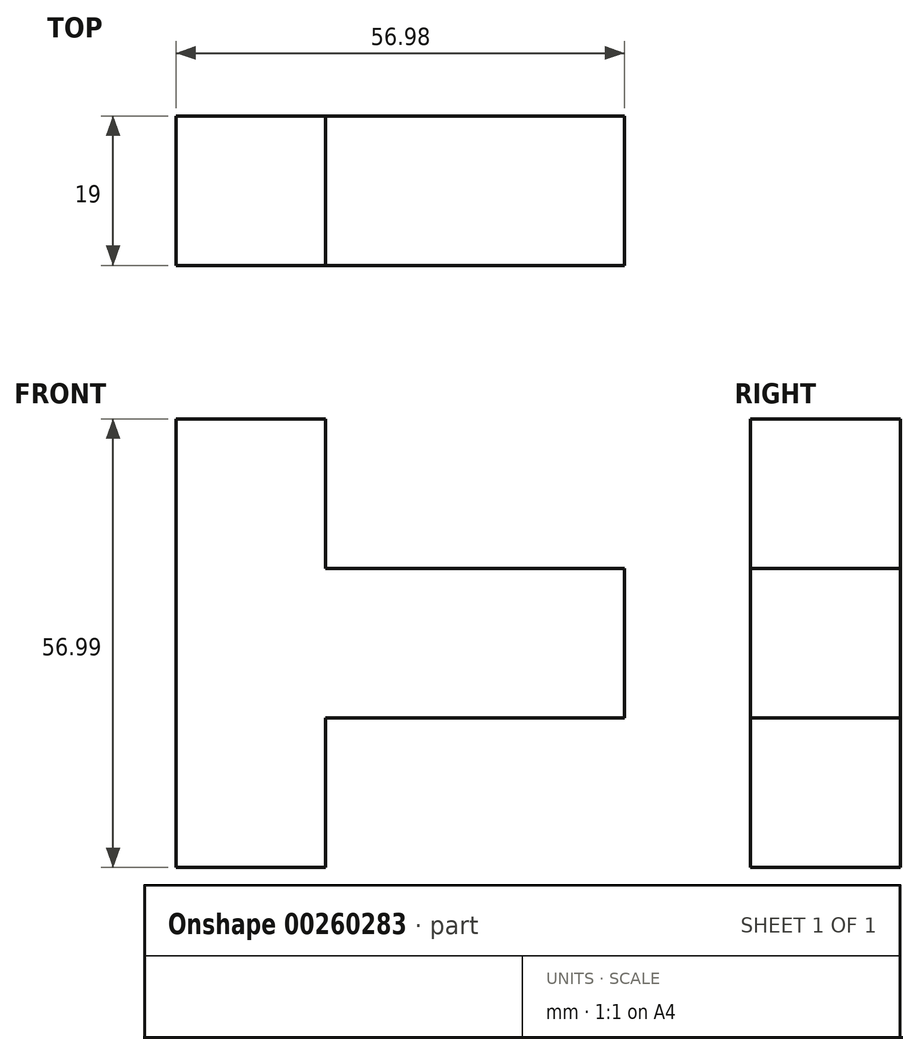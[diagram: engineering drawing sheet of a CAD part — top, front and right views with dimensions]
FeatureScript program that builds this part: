
annotation { "Feature Type Name" : "Feature", "Feature Type Description" : "" }
export const myFeature = defineFeature(function(context is Context, id is Id, definition is map)
    precondition{}
    {
        {
            var Q0;
            Q0=qCreatedBy(makeId("Front.planeOp"),FACE);
            var sketch = newSketch(context, id + "F0", { "sketchPlane" : qUnion([Q0])});
            skLineSegment(sketch, "E0.bottom", {"start": v(-67.92, 0) * mm, "end": v(-48.93, 0) * mm});
            skLineSegment(sketch, "E0.top", {"start": v(-67.92, -19) * mm, "end": v(-48.93, -19) * mm});
            skLineSegment(sketch, "E0.left", {"start": v(-67.92, 0) * mm, "end": v(-67.92, -19) * mm});
            skLineSegment(sketch, "E0.right", {"start": v(-48.93, 0) * mm, "end": v(-48.93, -19) * mm});
            skLineSegment(sketch, "E1.top", {"start": v(-67.92, -38) * mm, "end": v(-48.93, -38) * mm});
            skLineSegment(sketch, "E1.left", {"start": v(-67.92, -19) * mm, "end": v(-67.92, -38) * mm});
            skLineSegment(sketch, "E1.right", {"start": v(-48.93, -19) * mm, "end": v(-48.93, -38) * mm});
            skLineSegment(sketch, "E2.top", {"start": v(-67.92, 19) * mm, "end": v(-48.93, 19) * mm});
            skLineSegment(sketch, "E2.left", {"start": v(-67.92, 0) * mm, "end": v(-67.92, 19) * mm});
            skLineSegment(sketch, "E2.right", {"start": v(-48.93, 0) * mm, "end": v(-48.93, 19) * mm});
            skLineSegment(sketch, "E3.bottom", {"start": v(-48.93, 0) * mm, "end": v(-29.93, 0) * mm});
            skLineSegment(sketch, "E3.top", {"start": v(-48.93, -19) * mm, "end": v(-29.93, -19) * mm});
            skLineSegment(sketch, "E3.right", {"start": v(-29.93, 0) * mm, "end": v(-29.93, -19) * mm});
            skLineSegment(sketch, "E4.bottom", {"start": v(-29.93, 0) * mm, "end": v(-10.94, 0) * mm});
            skLineSegment(sketch, "E4.top", {"start": v(-29.93, -19) * mm, "end": v(-10.94, -19) * mm});
            skLineSegment(sketch, "E4.right", {"start": v(-10.94, 0) * mm, "end": v(-10.94, -19) * mm});
            skLineSegment(sketch, "E5.bottom", {"start": v(-10.94, -19) * mm, "end": v(-29.93, -19) * mm});
            skLineSegment(sketch, "E5.top", {"start": v(-10.94, -38) * mm, "end": v(-29.93, -38) * mm});
            skLineSegment(sketch, "E5.left", {"start": v(-10.94, -19) * mm, "end": v(-10.94, -38) * mm});
            skLineSegment(sketch, "E5.right", {"start": v(-29.93, -19) * mm, "end": v(-29.93, -38) * mm});
            skSolve(sketch);
        }
        {
            var Q0;
            Q0=makeQuery(id+"F0.imprint","IMPRINT",FACE,{"disambiguationData":[TD([[makeQuery(id+"F0.imprint","IMPRINT",EDGE,{"derivedFrom":sQuery(id+"F0.wireOp",EDGE,"E0.top")}),-1.0]])]});
            var Q1;
            Q1=makeQuery(id+"F0.imprint","IMPRINT",FACE,{"disambiguationData":[TD([[makeQuery(id+"F0.imprint","IMPRINT",EDGE,{"derivedFrom":sQuery(id+"F0.wireOp",EDGE,"E0.bottom")}),1.0]])]});
            var Q2;
            Q2=makeQuery(id+"F0.imprint","IMPRINT",FACE,{"disambiguationData":[TD([[makeQuery(id+"F0.imprint","IMPRINT",EDGE,{"derivedFrom":sQuery(id+"F0.wireOp",EDGE,"E0.left")}),1.0]])]});
            var Q3;
            Q3=makeQuery(id+"F0.imprint","IMPRINT",FACE,{"disambiguationData":[TD([[makeQuery(id+"F0.imprint","IMPRINT",EDGE,{"derivedFrom":sQuery(id+"F0.wireOp",EDGE,"E3.bottom")}),-1.0]])]});
            var Q4;
            Q4=makeQuery(id+"F0.imprint","IMPRINT",FACE,{"disambiguationData":[TD([[makeQuery(id+"F0.imprint","IMPRINT",EDGE,{"derivedFrom":sQuery(id+"F0.wireOp",EDGE,"E4.bottom")}),-1.0]])]});
            var Q5;
            Q5=makeQuery(id+"F0.imprint","IMPRINT",FACE,{"disambiguationData":[TD([[makeQuery(id+"F0.imprint","IMPRINT",EDGE,{"derivedFrom":sQuery(id+"F0.wireOp",EDGE,"E5.bottom")}),1.0]])]});
            extrude(context, id + "F1", {"entities" : qUnion([Q0, Q1, Q2, Q3, Q4, Q5]), "depth" : 19 * mm});
        }
    });
